FCSTD DOCUMENT  (FreeCAD 0.19R24291 (Git))
Label: shack
License: All rights reserved
LicenseURL: http://en.wikipedia.org/wiki/All_rights_reserved
objects: Sketcher::SketchObject×2
note: 2 computed .brp shape members not serialized (recipe doc carries the construction recipe); baked Part::Feature solids carry a one-line shape summary decoded from their .brp

FEATURE [Sketcher::SketchObject] Sketch
  FullyConstrained = false
  expr: Constraints[44] = .Constraints.wall_dist
  sketch-geometry (15):
    g0: LineSegment StartX=0 StartY=0 StartZ=0 EndX=2947 EndY=0 EndZ=0
    g1: LineSegment StartX=2947 StartY=0 StartZ=0 EndX=2947 EndY=3615 EndZ=0
    g2: LineSegment StartX=2947 StartY=3615 StartZ=0 EndX=0 EndY=3615 EndZ=0
    g3: LineSegment StartX=0 StartY=3615 StartZ=0 EndX=0 EndY=0 EndZ=0
    g4: LineSegment StartX=2947 StartY=1645 StartZ=0 EndX=2947 EndY=665 EndZ=0
    g5: LineSegment StartX=1985 StartY=3615 StartZ=0 EndX=2947 EndY=3615 EndZ=0
    g6: LineSegment StartX=527 StartY=3557 StartZ=0 EndX=2947 EndY=3557 EndZ=0
    g7: LineSegment StartX=2947 StartY=3557 StartZ=0 EndX=2947 EndY=2957 EndZ=0
    g8: LineSegment StartX=2947 StartY=2957 StartZ=0 EndX=527 EndY=2957 EndZ=0
    g9: LineSegment StartX=527 StartY=2957 StartZ=0 EndX=527 EndY=3557 EndZ=0
    g10: LineSegment StartX=2947 StartY=573.627 StartZ=0 EndX=0 EndY=573.627 EndZ=0
    g11: LineSegment StartX=58 StartY=3557 StartZ=0 EndX=658 EndY=3557 EndZ=0
    g12: LineSegment StartX=658 StartY=3557 StartZ=0 EndX=658 EndY=1137 EndZ=0
    g13: LineSegment StartX=658 StartY=1137 StartZ=0 EndX=58 EndY=1137 EndZ=0
    g14: LineSegment StartX=58 StartY=1137 StartZ=0 EndX=58 EndY=3557 EndZ=0
  constraints (47):
    c: Coincident(g0,g1)
    c: Coincident(g1,g2)
    c: Coincident(g2,g3)
    c: Coincident(g3,g0)
    c: Horizontal(g0)
    c: Horizontal(g2)
    c: Vertical(g1)
    c: Vertical(g3)
    c: Coincident(g0,g-1)
    c: DistanceY(g3,g3) = 3615
    c: DistanceX(g2,g2) = 2947
    c: PointOnObject(g4,g1)
    c: PointOnObject(g4,g1)
    c: DistanceY(g4,g4) = 980
    c: DistanceY(g4,g1) = 1970
    c: PointOnObject(g5,g2)
    c: Coincident(g5,g1)
    c: DistanceX(g5,g1) = 962
    c: Coincident(g6,g7)
    c: Coincident(g7,g8)
    c: Coincident(g8,g9)
    c: Coincident(g9,g6)
    c: Horizontal(g6)
    c: Horizontal(g8)
    c: Vertical(g7)
    c: Vertical(g9)
    c: DistanceX(g6,g6) = 2420
    c: DistanceY(g7,g7) = 600
    c: PointOnObject(g10,g1)
    c: PointOnObject(g10,g3)
    c: Horizontal(g10)
    c: Coincident(g11,g12)
    c: Coincident(g12,g13)
    c: Coincident(g13,g14)
    c: Coincident(g14,g11)
    c: Horizontal(g11)
    c: Horizontal(g13)
    c: Vertical(g12)
    c: Vertical(g14)
    c: Equal(g11,g9)
    c: Equal(g12,g8)
    c: PointOnObject(g11,g6)
    c: PointOnObject(g7,g1)
    c: DistanceX(g2,g11) = 58  'wall_dist'
    c: DistanceY(g11,g2) = 58
    c: DistanceY(g10,g13) = 563.373
    c: DistanceY(g10,g8) = 2383.37
FEATURE [Sketcher::SketchObject] Sketch001
  ExternalGeometry = -> [Sketch]
  FullyConstrained = false
  MapMode = 2
  Support = -> [Sketch]
  sketch-geometry (5):
    g0: LineSegment StartX=729.378 StartY=3615 StartZ=0 EndX=1329.38 EndY=3615 EndZ=0
    g1: LineSegment StartX=1329.38 StartY=3615 StartZ=0 EndX=1929.38 EndY=3615 EndZ=0
    g2: LineSegment StartX=0 StartY=3043.79 StartZ=0 EndX=0 EndY=2443.79 EndZ=0
    g3: LineSegment StartX=0 StartY=2443.79 StartZ=0 EndX=0 EndY=1843.79 EndZ=0
    g4: LineSegment StartX=0 StartY=1843.79 StartZ=0 EndX=0 EndY=1243.79 EndZ=0
  constraints (12):
    c: PointOnObject(g0,g-3)
    c: Coincident(g1,g0)
    c: PointOnObject(g2,g-4)
    c: Coincident(g3,g2)
    c: Coincident(g4,g3)
    c: PointOnObject(g2,g-4)
    c: PointOnObject(g3,g-4)
    c: PointOnObject(g4,g-4)
    c: PointOnObject(g0,g-3)
    c: PointOnObject(g1,g-3)
    c: Equal(g0, g1-g4) x4
    c: DistanceX(g0,g0) = 600
